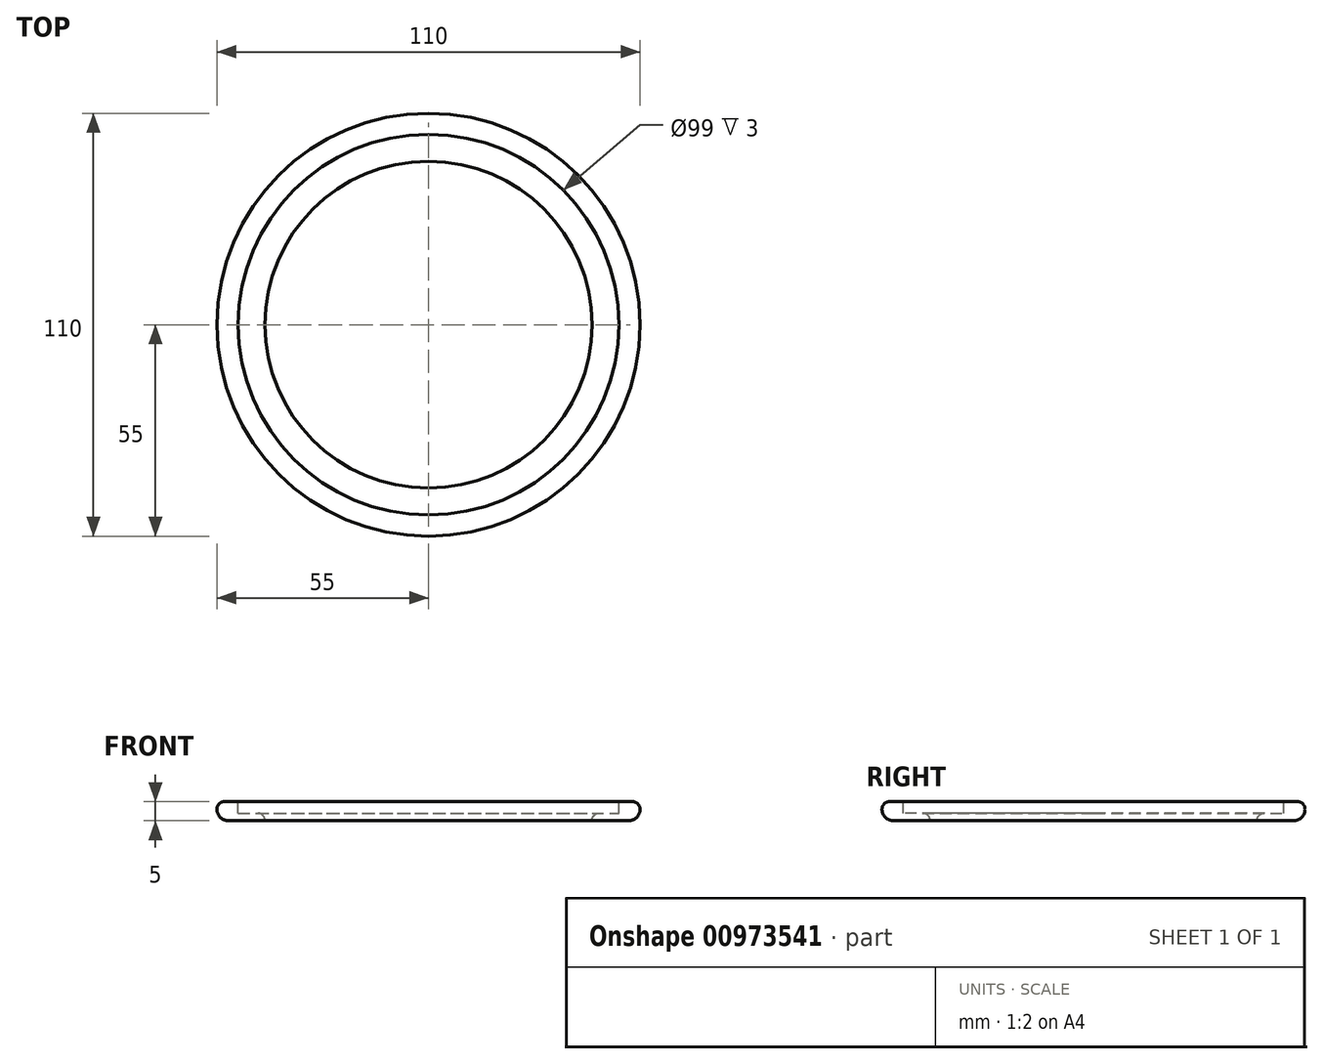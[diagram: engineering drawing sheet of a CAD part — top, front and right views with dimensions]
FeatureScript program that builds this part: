
annotation { "Feature Type Name" : "Feature", "Feature Type Description" : "" }
export const myFeature = defineFeature(function(context is Context, id is Id, definition is map)
    precondition{}
    {
        {
            var Q0;
            Q0=qCreatedBy(makeId("Top.planeOp"),FACE);
            var sketch = newSketch(context, id + "F0", { "sketchPlane" : qUnion([Q0])});
            skCircle(sketch, "E0", {"center": v(0, 0) * mm, "radius": 55 * mm});
            skSolve(sketch);
        }
        {
            var Q0;
            Q0=makeQuery(id+"F0.imprint","IMPRINT",FACE,{"disambiguationData":[TD([[makeQuery(id+"F0.imprint","IMPRINT",EDGE,{"derivedFrom":sQuery(id+"F0.wireOp",EDGE,"E0")}),1.0]])]});
            extrude(context, id + "F1", {"entities" : qUnion([Q0]), "oppositeDirection" : true, "depth" : 5 * mm, "offsetDistance" : 25 * mm});
        }
        {
            var Q0;
            Q0=makeQuery(id+"F1.opExtrude","CAP_EDGE",EDGE,{"disambiguationData":[OSD([sQuery(id+"F0.wireOp",EDGE,"E0")])],"isStart":false});
            fillet(context, id + "F2", {"entities" : qUnion([Q0]), "radius" : 3 * mm, "tangentPropagation" : true, "allowEdgeOverflow" : false});
        }
        {
            var Q0;
            Q0=makeQuery(id+"F1.opExtrude","CAP_EDGE",EDGE,{"disambiguationData":[OSD([sQuery(id+"F0.wireOp",EDGE,"E0")])],"isStart":true});
            fillet(context, id + "F3", {"entities" : qUnion([Q0]), "radius" : 2 * mm, "tangentPropagation" : true, "allowEdgeOverflow" : false});
        }
        {
            var Q0;
            Q0=qCreatedBy(makeId("Top.planeOp"),FACE);
            var sketch = newSketch(context, id + "F4", { "sketchPlane" : qUnion([Q0])});
            skCircle(sketch, "E1", {"center": v(0, 0) * mm, "radius": 49.5 * mm});
            skSolve(sketch);
        }
        {
            var Q0;
            Q0=makeQuery(id+"F4.imprint","IMPRINT",FACE,{"disambiguationData":[TD([[makeQuery(id+"F4.imprint","IMPRINT",EDGE,{"derivedFrom":sQuery(id+"F4.wireOp",EDGE,"E1")}),1.0]])]});
            var Q1;
            Q1=sQuery(id+"F4.wireOp",EDGE,"E1");
            extrude(context, id + "F5", {"entities" : qUnion([Q0]), "operationType" : NewBodyOperationType.REMOVE, "surfaceEntities" : qUnion([Q1]), "oppositeDirection" : true, "depth" : 5 * mm, "offsetDistance" : 25 * mm});
        }
        {
            var Q0;
            Q0=makeQuery(id+"F1.opExtrude","CAP_FACE",FACE,{"disambiguationData":[OSD([sQuery(id+"F0.wireOp",EDGE,"E0")])],"isStart":false});
            var sketch = newSketch(context, id + "F6", { "sketchPlane" : qUnion([Q0])});
            skCircle(sketch, "E2.0", {"center": v(0, 0) * mm, "radius": 42.5 * mm});
            skSolve(sketch);
        }
        {
            var Q0;
            Q0=makeQuery(id+"F6.imprint","IMPRINT",FACE,{"disambiguationData":[TD([[makeQuery(id+"F6.imprint","IMPRINT",EDGE,{"derivedFrom":sQuery(id+"F6.wireOp",EDGE,"E2.0")}),-1.0]])]});
            extrude(context, id + "F7", {"entities" : qUnion([Q0]), "operationType" : NewBodyOperationType.ADD, "oppositeDirection" : true, "depth" : 2 * mm, "offsetDistance" : 25 * mm});
        }
        {
            var Q0;
            Q0=makeQuery(id+"F7.opExtrude","CAP_EDGE",EDGE,{"disambiguationData":[OSD([sQuery(id+"F6.wireOp",EDGE,"E2.0")])],"isStart":false});
            fillet(context, id + "F8", {"entities" : qUnion([Q0]), "radius" : 2 * mm, "tangentPropagation" : true, "allowEdgeOverflow" : false});
        }
    });
